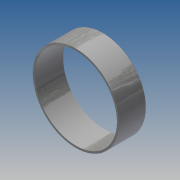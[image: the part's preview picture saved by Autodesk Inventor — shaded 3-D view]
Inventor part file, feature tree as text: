
AUTODESK INVENTOR PART (.ipt)
format: ipt  version: 2017.3 (Build 213257000, 257)  size: 169,984 bytes
history: native  units: in
note: dims shown in document units (in); Inventor stores cm internally (conversion verified against a paired STEP export)
features: chamfer x2, plane x2, split x2, extrude x1, sketch x1
ambient origin geometry x8: Origin, YZ Plane, XZ Plane, XY Plane, X Axis, Y Axis, Z Axis, Center Point
bodies: Solid1 (feature_tree)
feature tree (8):
  extrude  "Extrusion1"  Depth=10.5312in
  chamfer  "Chamfer1"  Distance=10.5312in
  plane  "Work Plane2"
  split  "Split1"
  split  "Split2"
  chamfer  "Chamfer2"  Distance=0.6875in
  sketch  "Sketch1"  dims[d0=32.0in d1=30.5in d2=10.5312in d3=0.0in d4=0.6875in d5=0.125in d6=0.2577in d7=-2.0in d8=0.75in d9=0.0312in d10=0.125in d11=45.0deg]
  plane  "Work Plane1"
